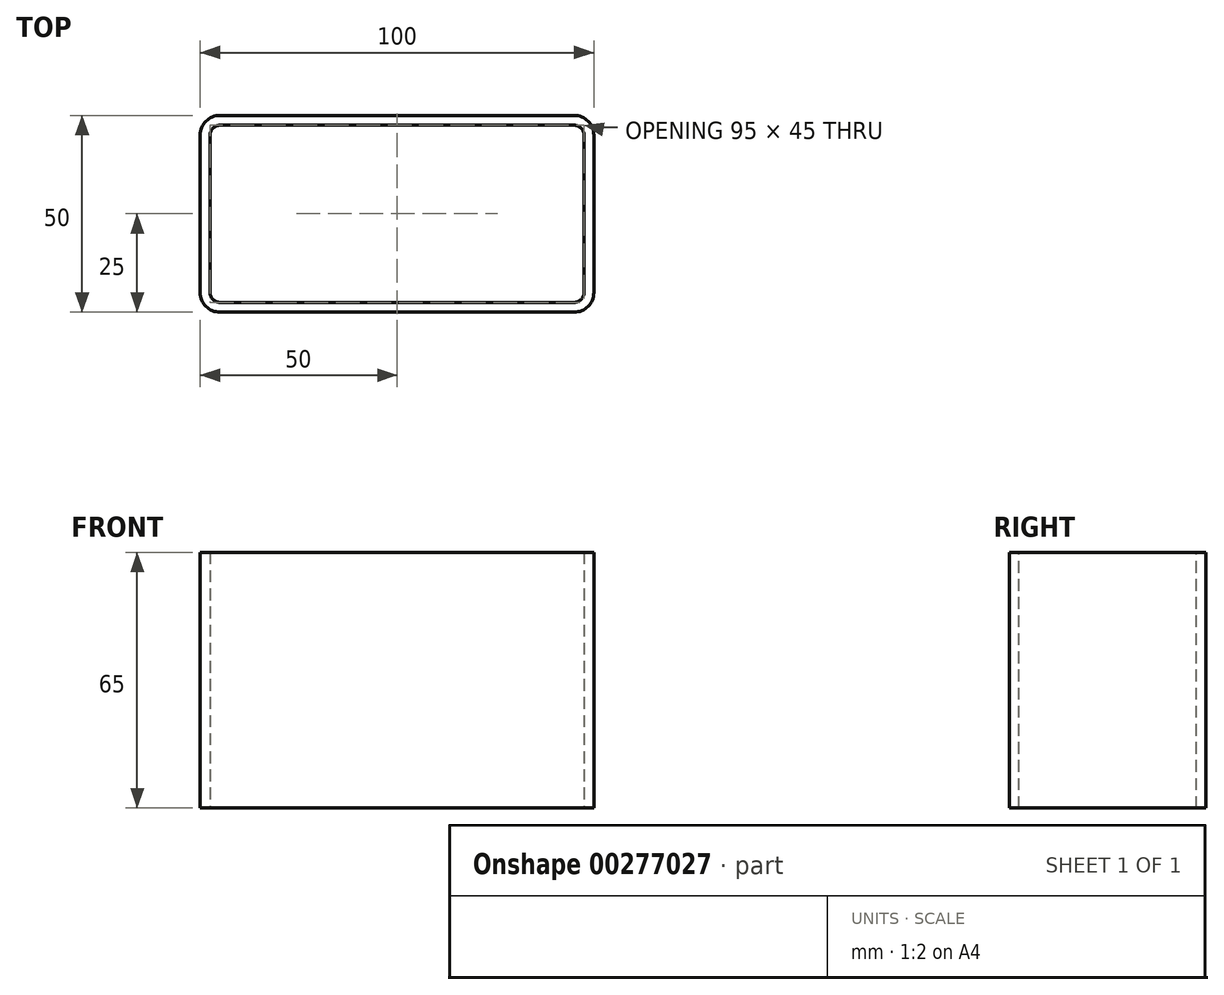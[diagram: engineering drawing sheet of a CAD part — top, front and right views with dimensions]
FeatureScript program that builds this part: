
annotation { "Feature Type Name" : "Feature", "Feature Type Description" : "" }
export const myFeature = defineFeature(function(context is Context, id is Id, definition is map)
    precondition{}
    {
        {
            var Q0;
            Q0=qCreatedBy(makeId("Front.planeOp"),FACE);
            var sketch = newSketch(context, id + "F0", { "sketchPlane" : qUnion([Q0])});
            skLineSegment(sketch, "E0.bottom", {"start": v(50, 32.5) * mm, "end": v(-50, 32.5) * mm});
            skLineSegment(sketch, "E0.top", {"start": v(50, -32.5) * mm, "end": v(-50, -32.5) * mm});
            skLineSegment(sketch, "E0.left", {"start": v(50, 32.5) * mm, "end": v(50, -32.5) * mm});
            skLineSegment(sketch, "E0.right", {"start": v(-50, 32.5) * mm, "end": v(-50, -32.5) * mm});
            skPoint(sketch, "E0.middle", {"position": v(0, 0) * mm});
            skSolve(sketch);
        }
        {
            var Q0;
            Q0 = qSketchRegion(id + "F0", true);
            extrude(context, id + "F1", {"entities" : qUnion([Q0]), "depth" : 50 * mm});
        }
        {
            var Q0;
            Q0=makeQuery(id+"F1.opExtrude","CAP_EDGE",EDGE,{"disambiguationData":[OSD([sQuery(id+"F0.wireOp",EDGE,"E0.right")])],"isStart":false});
            var Q1;
            Q1=makeQuery(id+"F1.opExtrude","CAP_EDGE",EDGE,{"disambiguationData":[OSD([sQuery(id+"F0.wireOp",EDGE,"E0.left")])],"isStart":false});
            var Q2;
            Q2=makeQuery(id+"F1.opExtrude","CAP_EDGE",EDGE,{"disambiguationData":[OSD([sQuery(id+"F0.wireOp",EDGE,"E0.right")])],"isStart":true});
            var Q3;
            Q3=makeQuery(id+"F1.opExtrude","CAP_EDGE",EDGE,{"disambiguationData":[OSD([sQuery(id+"F0.wireOp",EDGE,"E0.left")])],"isStart":true});
            fillet(context, id + "F2", {"entities" : qUnion([Q0, Q1, Q2, Q3]), "radius" : 5 * mm, "tangentPropagation" : true, "allowEdgeOverflow" : false});
        }
        {
            var Q0;
            Q0=makeQuery(id+"F1.opExtrude","SWEPT_FACE",FACE,{"disambiguationData":[OSD([sQuery(id+"F0.wireOp",EDGE,"E0.bottom")])]});
            var Q1;
            Q1=makeQuery(id+"F1.opExtrude","SWEPT_FACE",FACE,{"disambiguationData":[OSD([sQuery(id+"F0.wireOp",EDGE,"E0.top")])]});
            shell(context, id + "F3", {"entities" : qUnion([Q0, Q1]), "thickness" : 2.5 * mm});
        }
    });
